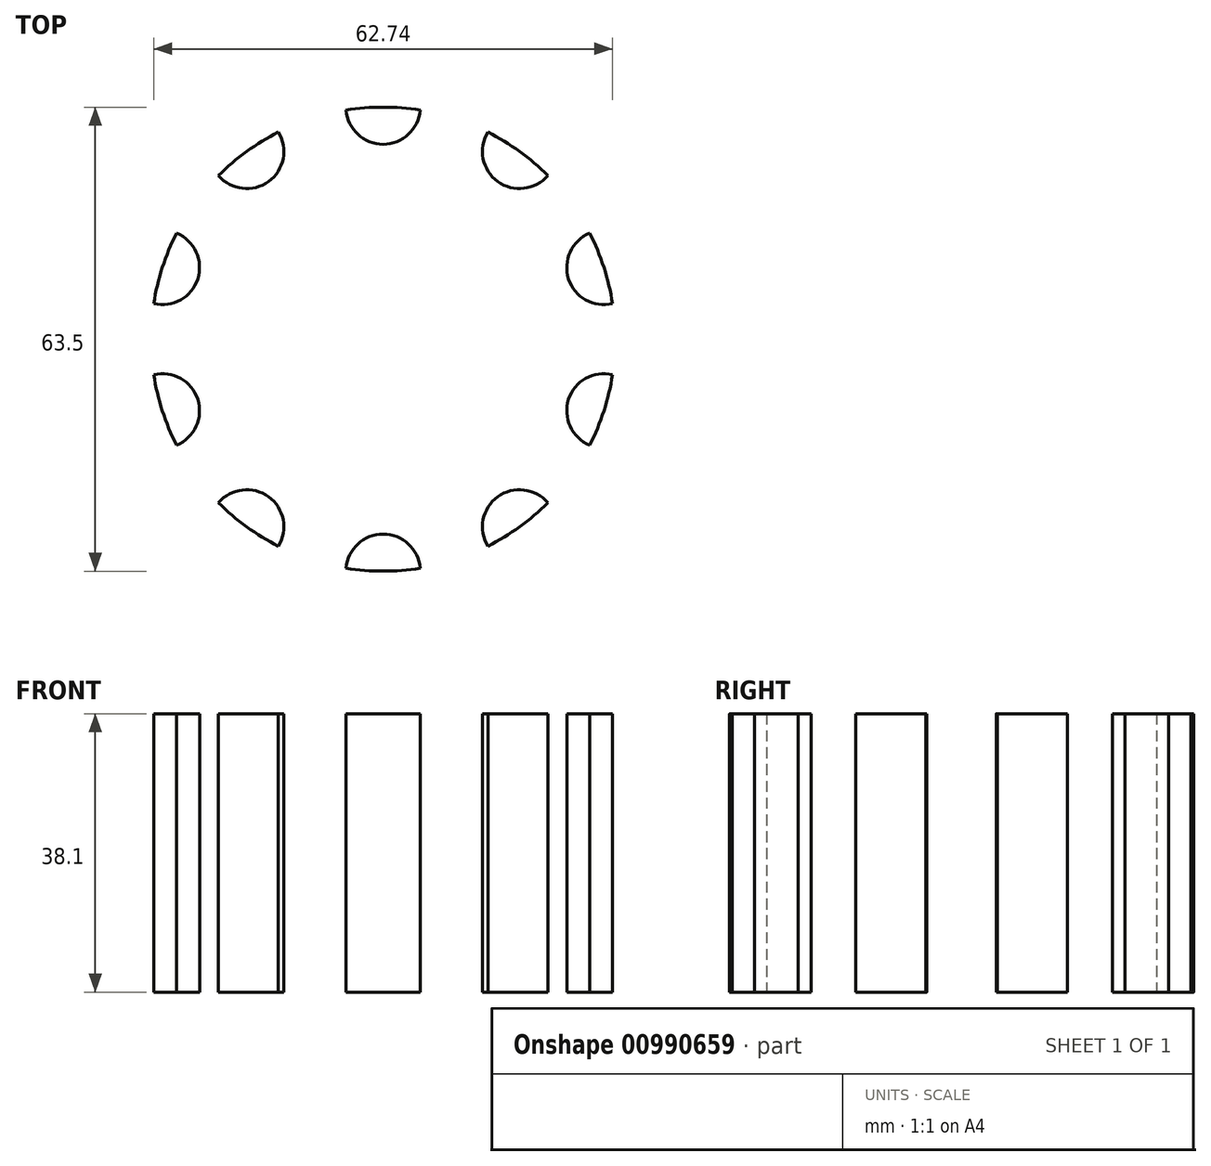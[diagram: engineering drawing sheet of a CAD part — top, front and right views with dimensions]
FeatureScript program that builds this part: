
annotation { "Feature Type Name" : "Feature", "Feature Type Description" : "" }
export const myFeature = defineFeature(function(context is Context, id is Id, definition is map)
    precondition{}
    {
        {
            var Q0;
            Q0=qCreatedBy(makeId("Top.planeOp"),FACE);
            var sketch = newSketch(context, id + "F0", { "sketchPlane" : qUnion([Q0])});
            skCircle(sketch, "E0", {"center": v(0, 0) * mm, "radius": 31.75 * mm});
            skSolve(sketch);
        }
        {
            var Q0;
            Q0=makeQuery(id+"F0.imprint","IMPRINT",FACE,{"disambiguationData":[TD([[makeQuery(id+"F0.imprint","IMPRINT",EDGE,{"derivedFrom":sQuery(id+"F0.wireOp",EDGE,"E0")}),1.0]])]});
            extrude(context, id + "F1", {"entities" : qUnion([Q0]), "depth" : 38.1 * mm});
        }
        {
            var Q0;
            Q0=qCreatedBy(makeId("Top.planeOp"),FACE);
            var sketch = newSketch(context, id + "F2", { "sketchPlane" : qUnion([Q0])});
            skCircle(sketch, "E1", {"center": v(0, 31.75) * mm, "radius": 5.08 * mm});
            skCircle(sketch, "E2.1.0", {"center": v(-18.66, 25.69) * mm, "radius": 5.08 * mm});
            skCircle(sketch, "E2.2.0", {"center": v(-30.2, 9.81) * mm, "radius": 5.08 * mm});
            skCircle(sketch, "E2.3.0", {"center": v(-30.2, -9.81) * mm, "radius": 5.08 * mm});
            skCircle(sketch, "E2.4.0", {"center": v(-18.66, -25.69) * mm, "radius": 5.08 * mm});
            skCircle(sketch, "E2.5.0", {"center": v(0, -31.75) * mm, "radius": 5.08 * mm});
            skCircle(sketch, "E2.6.0", {"center": v(18.66, -25.69) * mm, "radius": 5.08 * mm});
            skCircle(sketch, "E2.7.0", {"center": v(30.2, -9.81) * mm, "radius": 5.08 * mm});
            skCircle(sketch, "E2.8.0", {"center": v(30.2, 9.81) * mm, "radius": 5.08 * mm});
            skCircle(sketch, "E2.9.0", {"center": v(18.66, 25.69) * mm, "radius": 5.08 * mm});
            skPoint(sketch, "E2.center", {"position": v(0, 0) * mm});
            skSolve(sketch);
        }
        {
            var Q0;
            Q0=qSketchRegion(id+"F2",true);
            extrude(context, id + "F3", {"entities" : qUnion([Q0]), "depth" : 50.8 * mm});
        }
        {
            var Q0;
            Q0=makeQuery(id+"F3.opExtrude","SWEPT_BODY",BODY,{"disambiguationData":[OSD([sQuery(id+"F2.wireOp",EDGE,"E2.5.0")])]});
            var Q1;
            Q1=makeQuery(id+"F1.opExtrude","SWEPT_BODY",BODY,{"disambiguationData":[OSD([sQuery(id+"F0.wireOp",EDGE,"E0")])]});
            booleanBodies(context, id + "F4", {"operationType" : BooleanOperationType.INTERSECTION, "tools" : qUnion([Q0, Q1]), "keepTools" : true});
        }
        {
            var Q0;
            Q0=makeQuery(id+"F3.opExtrude","SWEPT_BODY",BODY,{"disambiguationData":[OSD([sQuery(id+"F2.wireOp",EDGE,"E2.6.0")])]});
            var Q1;
            Q1=makeQuery(id+"F1.opExtrude","SWEPT_BODY",BODY,{"disambiguationData":[OSD([sQuery(id+"F0.wireOp",EDGE,"E0")])]});
            booleanBodies(context, id + "F5", {"operationType" : BooleanOperationType.INTERSECTION, "tools" : qUnion([Q0, Q1]), "keepTools" : true});
        }
        {
            var Q0;
            Q0=makeQuery(id+"F3.opExtrude","SWEPT_BODY",BODY,{"disambiguationData":[OSD([sQuery(id+"F2.wireOp",EDGE,"E2.7.0")])]});
            var Q1;
            Q1=makeQuery(id+"F1.opExtrude","SWEPT_BODY",BODY,{"disambiguationData":[OSD([sQuery(id+"F0.wireOp",EDGE,"E0")])]});
            booleanBodies(context, id + "F6", {"operationType" : BooleanOperationType.INTERSECTION, "tools" : qUnion([Q0, Q1]), "keepTools" : true});
        }
        {
            var Q0;
            Q0=makeQuery(id+"F3.opExtrude","SWEPT_BODY",BODY,{"disambiguationData":[OSD([sQuery(id+"F2.wireOp",EDGE,"E2.8.0")])]});
            var Q1;
            Q1=makeQuery(id+"F1.opExtrude","SWEPT_BODY",BODY,{"disambiguationData":[OSD([sQuery(id+"F0.wireOp",EDGE,"E0")])]});
            booleanBodies(context, id + "F7", {"operationType" : BooleanOperationType.INTERSECTION, "tools" : qUnion([Q0, Q1]), "keepTools" : true});
        }
        {
            var Q0;
            Q0=makeQuery(id+"F3.opExtrude","SWEPT_BODY",BODY,{"disambiguationData":[OSD([sQuery(id+"F2.wireOp",EDGE,"E2.9.0")])]});
            var Q1;
            Q1=makeQuery(id+"F1.opExtrude","SWEPT_BODY",BODY,{"disambiguationData":[OSD([sQuery(id+"F0.wireOp",EDGE,"E0")])]});
            booleanBodies(context, id + "F8", {"operationType" : BooleanOperationType.INTERSECTION, "tools" : qUnion([Q0, Q1]), "keepTools" : true});
        }
        {
            var Q0;
            Q0=makeQuery(id+"F3.opExtrude","SWEPT_BODY",BODY,{"disambiguationData":[OSD([sQuery(id+"F2.wireOp",EDGE,"E1")])]});
            var Q1;
            Q1=makeQuery(id+"F1.opExtrude","SWEPT_BODY",BODY,{"disambiguationData":[OSD([sQuery(id+"F0.wireOp",EDGE,"E0")])]});
            booleanBodies(context, id + "F9", {"operationType" : BooleanOperationType.INTERSECTION, "tools" : qUnion([Q0, Q1]), "keepTools" : true});
        }
        {
            var Q0;
            Q0=makeQuery(id+"F3.opExtrude","SWEPT_BODY",BODY,{"disambiguationData":[OSD([sQuery(id+"F2.wireOp",EDGE,"E2.1.0")])]});
            var Q1;
            Q1=makeQuery(id+"F1.opExtrude","SWEPT_BODY",BODY,{"disambiguationData":[OSD([sQuery(id+"F0.wireOp",EDGE,"E0")])]});
            booleanBodies(context, id + "F10", {"operationType" : BooleanOperationType.INTERSECTION, "tools" : qUnion([Q0, Q1]), "keepTools" : true});
        }
        {
            var Q0;
            Q0=makeQuery(id+"F3.opExtrude","SWEPT_BODY",BODY,{"disambiguationData":[OSD([sQuery(id+"F2.wireOp",EDGE,"E2.2.0")])]});
            var Q1;
            Q1=makeQuery(id+"F1.opExtrude","SWEPT_BODY",BODY,{"disambiguationData":[OSD([sQuery(id+"F0.wireOp",EDGE,"E0")])]});
            booleanBodies(context, id + "F11", {"operationType" : BooleanOperationType.INTERSECTION, "tools" : qUnion([Q0, Q1]), "keepTools" : true});
        }
        {
            var Q0;
            Q0=makeQuery(id+"F3.opExtrude","SWEPT_BODY",BODY,{"disambiguationData":[OSD([sQuery(id+"F2.wireOp",EDGE,"E2.3.0")])]});
            var Q1;
            Q1=makeQuery(id+"F1.opExtrude","SWEPT_BODY",BODY,{"disambiguationData":[OSD([sQuery(id+"F0.wireOp",EDGE,"E0")])]});
            booleanBodies(context, id + "F12", {"operationType" : BooleanOperationType.INTERSECTION, "tools" : qUnion([Q0, Q1]), "keepTools" : true});
        }
        {
            var Q0;
            Q0=makeQuery(id+"F3.opExtrude","SWEPT_BODY",BODY,{"disambiguationData":[OSD([sQuery(id+"F2.wireOp",EDGE,"E2.4.0")])]});
            var Q1;
            Q1=makeQuery(id+"F1.opExtrude","SWEPT_BODY",BODY,{"disambiguationData":[OSD([sQuery(id+"F0.wireOp",EDGE,"E0")])]});
            booleanBodies(context, id + "F13", {"operationType" : BooleanOperationType.INTERSECTION, "tools" : qUnion([Q0, Q1]), "keepTools" : true});
        }
        {
            var Q0;
            Q0=makeQuery(id+"F3.opExtrude","SWEPT_BODY",BODY,{"disambiguationData":[OSD([sQuery(id+"F2.wireOp",EDGE,"E2.5.0")])]});
            var Q1;
            Q1=makeQuery(id+"F3.opExtrude","SWEPT_BODY",BODY,{"disambiguationData":[OSD([sQuery(id+"F2.wireOp",EDGE,"E2.6.0")])]});
            var Q2;
            Q2=makeQuery(id+"F3.opExtrude","SWEPT_BODY",BODY,{"disambiguationData":[OSD([sQuery(id+"F2.wireOp",EDGE,"E2.7.0")])]});
            var Q3;
            Q3=makeQuery(id+"F3.opExtrude","SWEPT_BODY",BODY,{"disambiguationData":[OSD([sQuery(id+"F2.wireOp",EDGE,"E2.8.0")])]});
            var Q4;
            Q4=makeQuery(id+"F3.opExtrude","SWEPT_BODY",BODY,{"disambiguationData":[OSD([sQuery(id+"F2.wireOp",EDGE,"E2.9.0")])]});
            var Q5;
            Q5=makeQuery(id+"F3.opExtrude","SWEPT_BODY",BODY,{"disambiguationData":[OSD([sQuery(id+"F2.wireOp",EDGE,"E1")])]});
            var Q6;
            Q6=makeQuery(id+"F3.opExtrude","SWEPT_BODY",BODY,{"disambiguationData":[OSD([sQuery(id+"F2.wireOp",EDGE,"E2.1.0")])]});
            var Q7;
            Q7=makeQuery(id+"F3.opExtrude","SWEPT_BODY",BODY,{"disambiguationData":[OSD([sQuery(id+"F2.wireOp",EDGE,"E2.2.0")])]});
            var Q8;
            Q8=makeQuery(id+"F3.opExtrude","SWEPT_BODY",BODY,{"disambiguationData":[OSD([sQuery(id+"F2.wireOp",EDGE,"E2.3.0")])]});
            var Q9;
            Q9=makeQuery(id+"F3.opExtrude","SWEPT_BODY",BODY,{"disambiguationData":[OSD([sQuery(id+"F2.wireOp",EDGE,"E2.4.0")])]});
            var Q10;
            Q10=makeQuery(id+"F1.opExtrude","SWEPT_BODY",BODY,{"disambiguationData":[OSD([sQuery(id+"F0.wireOp",EDGE,"E0")])]});
            booleanBodies(context, id + "F14", {"operationType" : BooleanOperationType.INTERSECTION, "tools" : qUnion([Q0, Q1, Q2, Q3, Q4, Q5, Q6, Q7, Q8, Q9, Q10])});
        }
    });
